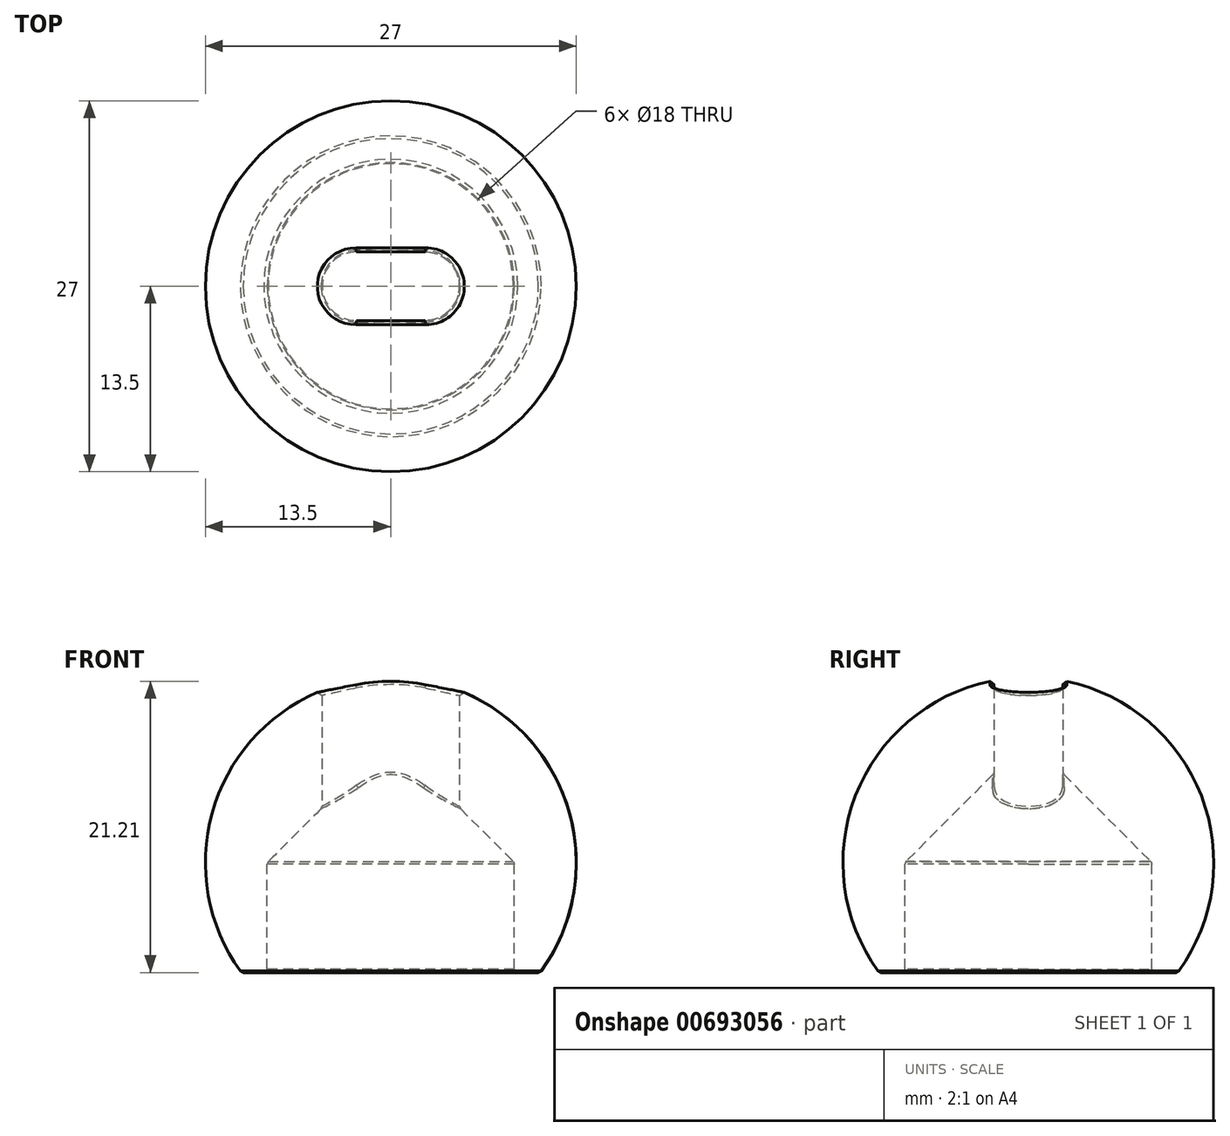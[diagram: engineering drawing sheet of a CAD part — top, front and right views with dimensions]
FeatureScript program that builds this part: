
annotation { "Feature Type Name" : "Feature", "Feature Type Description" : "" }
export const myFeature = defineFeature(function(context is Context, id is Id, definition is map)
    precondition{}
    {
        {
            var Q0;
            Q0=qCreatedBy(makeId("Front.planeOp"),FACE);
            var sketch = newSketch(context, id + "F0", { "sketchPlane" : qUnion([Q0])});
            skLineSegment(sketch, "E0", {"start": v(-10.87, -8) * mm, "end": v(-9, -8) * mm});
            skLineSegment(sketch, "E1", {"start": v(0, 13.5) * mm, "end": v(0, 9) * mm});
            skLineSegment(sketch, "E2", {"start": v(0, 9) * mm, "end": v(-9, 0) * mm});
            skLineSegment(sketch, "E3", {"start": v(-9, 0) * mm, "end": v(-9, -8) * mm});
            skArc(sketch, "E4", {"start": v(0, 13.5) * mm, "mid": v(-12.05, 6.1) * mm, "end": v(-10.87, -8) * mm});
            skArc(sketch, "E5", {"start": v(-10.87, -8) * mm, "mid": v(12.05, -6.1) * mm, "end": v(0, 13.5) * mm, "construction": true});
            skLineSegment(sketch, "E6", {"start": v(0, 13.5) * mm, "end": v(0, -13.5) * mm, "construction": true});
            skSolve(sketch);
        }
        {
            var Q0;
            Q0=qSketchRegion(id+"F0",true);
            var Q1;
            Q1=sQuery(id+"F0.wireOp",EDGE,"E6");
            revolve(context, id + "F1", {"entities" : qUnion([Q0]), "axis" : qUnion([Q1]), "revolveType" : RevolveType.FULL});
        }
        {
            var Q0;
            Q0=qCreatedBy(makeId("Top.planeOp"),FACE);
            var sketch = newSketch(context, id + "F2", { "sketchPlane" : qUnion([Q0])});
            skLineSegment(sketch, "E7", {"start": v(-2.5, 0) * mm, "end": v(2.5, 0) * mm, "construction": true});
            skPoint(sketch, "E8", {"position": v(0, 0) * mm});
            skArc(sketch, "E9.0.startCap", {"start": v(-2.5, -2.5) * mm, "mid": v(-5, 0) * mm, "end": v(-2.5, 2.5) * mm});
            skArc(sketch, "E9.0.endCap", {"start": v(2.5, 2.5) * mm, "mid": v(5, 0) * mm, "end": v(2.5, -2.5) * mm});
            skLineSegment(sketch, "E9.0.left", {"start": v(-2.5, 2.5) * mm, "end": v(2.5, 2.5) * mm});
            skLineSegment(sketch, "E9.0.right", {"start": v(-2.5, -2.5) * mm, "end": v(2.5, -2.5) * mm});
            skSolve(sketch);
        }
        {
            var Q0;
            Q0 = qSketchRegion(id + "F2", true);
            extrude(context, id + "F3", {"entities" : qUnion([Q0]), "operationType" : NewBodyOperationType.REMOVE, "depth" : 25 * mm, "offsetDistance" : 25 * mm});
        }
        {
            var Q0;
            Q0=makeQuery(id+"F1.opRevolve","SWEPT_EDGE",EDGE,{"disambiguationData":[OSD([sQuery(id+"F0.wireOp",EDGE,"E1"),sQuery(id+"F0.wireOp",EDGE,"E4")])]});
            var Q1;
            Q1=makeQuery(id+"F1.opRevolve","SWEPT_EDGE",EDGE,{"disambiguationData":[OSD([sQuery(id+"F0.wireOp",EDGE,"E0"),sQuery(id+"F0.wireOp",EDGE,"E3")])]});
            var Q2;
            Q2=makeQuery(id+"F1.opRevolve","SWEPT_EDGE",EDGE,{"disambiguationData":[OSD([sQuery(id+"F0.wireOp",EDGE,"E2"),sQuery(id+"F0.wireOp",EDGE,"E3")])]});
            var Q3;
            Q3=makeQuery(id+"F1.opRevolve","SWEPT_EDGE",EDGE,{"disambiguationData":[OSD([sQuery(id+"F0.wireOp",EDGE,"E1"),sQuery(id+"F0.wireOp",EDGE,"E2")])]});
            var Q4;
            Q4=makeQuery(id+"F1.opRevolve","SWEPT_EDGE",EDGE,{"disambiguationData":[OSD([sQuery(id+"F0.wireOp",EDGE,"E0"),sQuery(id+"F0.wireOp",EDGE,"E4")])]});
            var Q5;
            Q5=makeQuery(id+"F3.boolean.opBoolean","INTERSECT",EDGE,{"derivedFrom":[makeQuery(id+"F1.opRevolve","SWEPT_FACE",FACE,{"disambiguationData":[OSD([sQuery(id+"F0.wireOp",EDGE,"E4")])]}),makeQuery(id+"F3.opExtrude","SWEPT_FACE",FACE,{"disambiguationData":[OSD([sQuery(id+"F2.wireOp",EDGE,"E9.0.left")])]})]});
            var Q6;
            Q6=makeQuery(id+"F3.boolean.opBoolean","INTERSECT",EDGE,{"derivedFrom":[makeQuery(id+"F1.opRevolve","SWEPT_FACE",FACE,{"disambiguationData":[OSD([sQuery(id+"F0.wireOp",EDGE,"E2")])]}),makeQuery(id+"F3.opExtrude","SWEPT_FACE",FACE,{"disambiguationData":[OSD([sQuery(id+"F2.wireOp",EDGE,"E9.0.right")])]})]});
            chamfer(context, id + "F4", {"entities" : qUnion([Q0, Q1, Q2, Q3, Q4, Q5, Q6]), "width" : 0.25 * mm, "tangentPropagation" : true});
        }
    });
